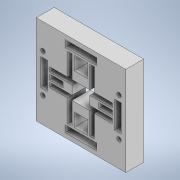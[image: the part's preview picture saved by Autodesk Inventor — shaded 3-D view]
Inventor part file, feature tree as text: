
AUTODESK INVENTOR PART (.ipt)
format: ipt  version: 2022 (Build 260153000, 153)  size: 226,816 bytes
history: native  units: in
note: dims shown in document units (in); Inventor stores cm internally (conversion verified against a paired STEP export)
features: extrude x5, sketch x5
ambient origin geometry x8: Origin, YZ Plane, XZ Plane, XY Plane, X Axis, Y Axis, Z Axis, Center Point
bodies: Solid1 (feature_tree)
feature tree (10):
  extrude  "Extrusion1"  Depth=5.0in
  extrude  "Extrusion2"  Depth=1.0in TaperAngle=0.0deg
  extrude  "Extrusion4"  Depth=1.0in
  extrude  "Extrusion3"  Depth=0.25in
  extrude  "Extrusion5"  Depth=0.1in
  sketch  "Sketch1"  dims[d0=5.0in d1=5.0in]
  sketch  "Sketch2"  dims[d2=0.25in d4=1.0in d5=0.0in]
  sketch  "Sketch3"  dims[d6=1.0in d7=1.0in]
  sketch  "Sketch4"  dims[d8=0.25in d9=0.25in]
  sketch  "Sketch5"  dims[d10=0.1in d11=0.1in d12=0.5in d13=0.75in d14=1.0in d15=0.0in d16=0.75in d17=0.125in d18=0.125in d19=0.75in d20=0.25in d21=0.25in d22=0.5in d23=1.0in d24=0.0in d25=1.5in d27=0.125in d28=0.25in d29=1.0in d30=0.0in d31=0.125in d32=0.25in d33=1.75in d34=1.0in d35=0.0in]
